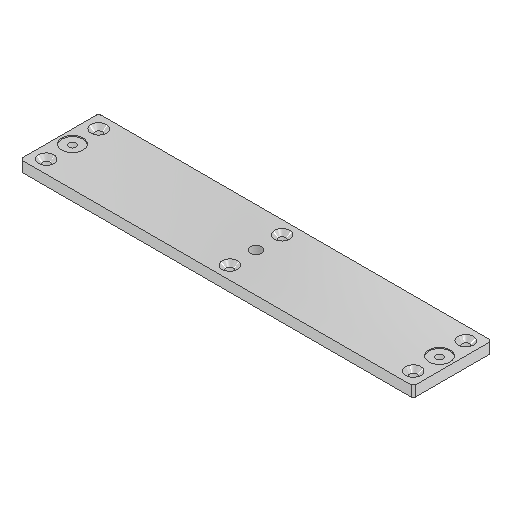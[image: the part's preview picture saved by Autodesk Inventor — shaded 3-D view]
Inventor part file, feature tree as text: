
AUTODESK INVENTOR PART (.ipt)
format: ipt  version: 2025.2 (Build 292293000, 293)  size: 135,680 bytes
history: native  units: in
note: dims shown in document units (in); Inventor stores cm internally (conversion verified against a paired STEP export)
features: hole x4, sketch x2, extrude x1, chamfer x1
ambient origin geometry x8: Origin, YZ Plane, XZ Plane, XY Plane, X Axis, Y Axis, Z Axis, Center Point
bodies: Solid1 (feature_tree)
feature tree (8):
  sketch  "Sketch1"  dims[d0=14.7638in d1=2.9528in]
  extrude  "Extrusion1"  Depth=2.9528in
  hole  "Hole1"  [1 undecoded]
  hole  "Hole2"  [1 undecoded]
  hole  "Hole3"  [1 undecoded]
  hole  "Hole4"  [1 undecoded]
  chamfer  "Chamfer1"  [1 undecoded]
  sketch  "Sketch2"  dims[d3=13.7795in d4=0.3937in d5=0.0in d11=0.2598in d12=0.875in d13=0.5709in d14=0.2677in d15=90.0deg d16=0.315in d17=0.8108in d18=0.0787in d19=0.0787in d20=45.0deg d23=0.4192in d24=0.9449in d25=0.4331in d26=0.2677in d27=90.0deg d28=0.315in d29=0.8108in d30=0.4921in d31=0.7874in d32=0.9449in d33=0.1575in d34=0.0787in d35=90.0deg d36=0.0394in d37=0.0in d38=0.2598in d39=0.2362in d40=0.5709in d41=0.0787in d42=90.0deg d43=0.0394in d44=0.0in d45=0.4921in]
note: 5 required parameter values undecoded (feature->parameter linkage not recoverable at this tier; creation-order binding heuristic only, values carry confidence <= 0.55)
